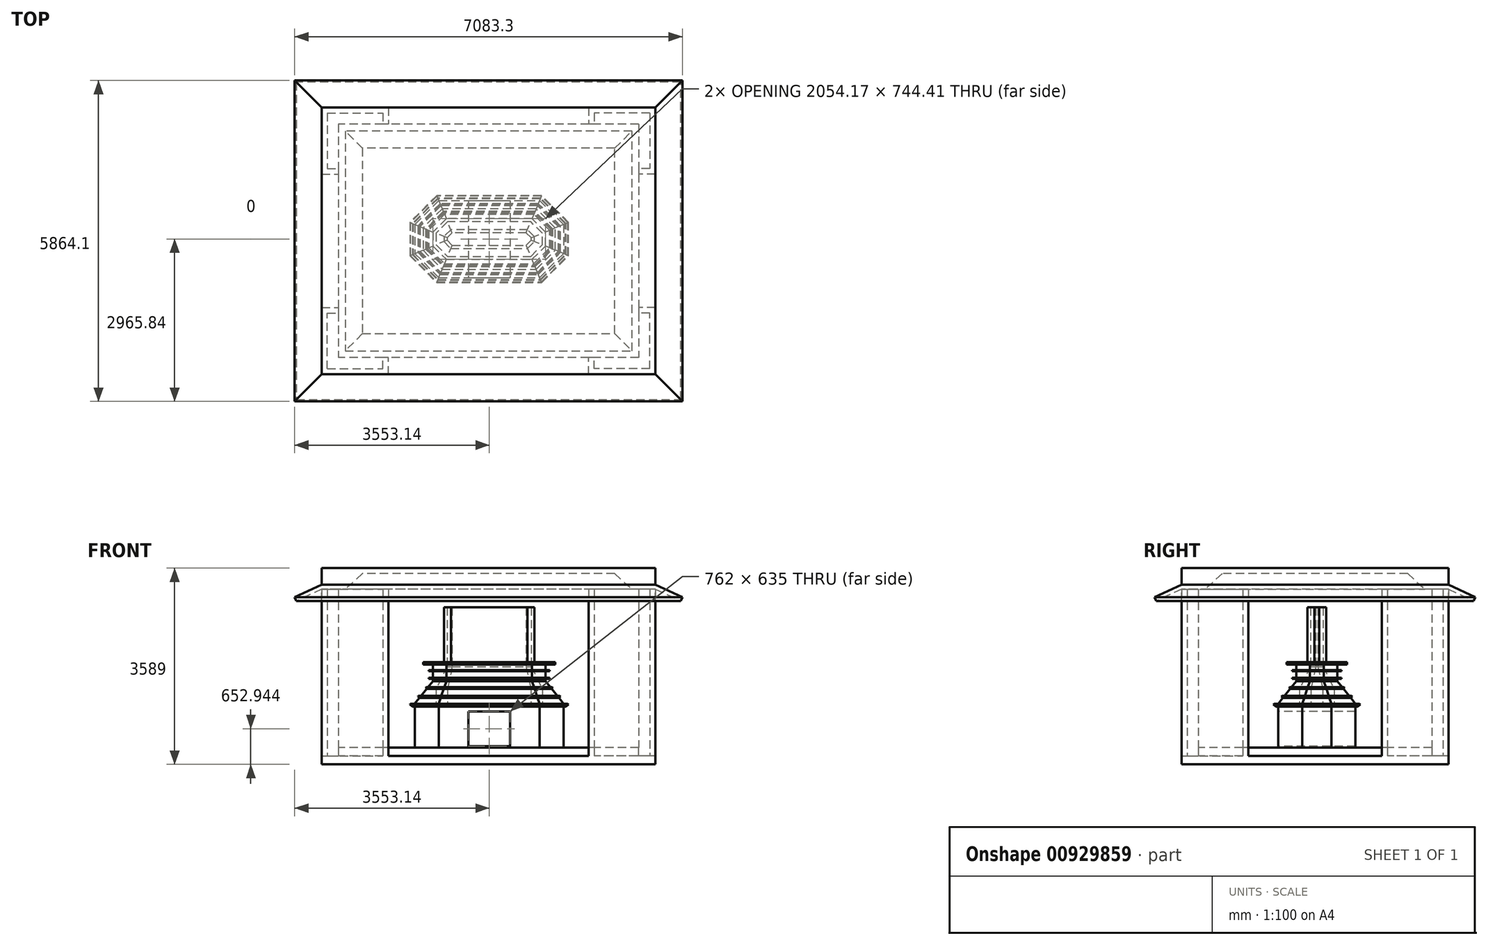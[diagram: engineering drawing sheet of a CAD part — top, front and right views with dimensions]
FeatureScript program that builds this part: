
annotation { "Feature Type Name" : "Feature", "Feature Type Description" : "" }
export const myFeature = defineFeature(function(context is Context, id is Id, definition is map)
    precondition{}
    {
        {
            var Q0;
            Q0=qCreatedBy(makeId("Right.planeOp"),FACE);
            var sketch = newSketch(context, id + "F0", { "sketchPlane" : qUnion([Q0])});
            skLineSegment(sketch, "E0", {"start": v(0, 0) * mm, "end": v(-2438.4, 0) * mm});
            skLineSegment(sketch, "E1", {"start": v(-2438.4, 0) * mm, "end": v(-2438.4, 152.4) * mm});
            skLineSegment(sketch, "E2", {"start": v(-2438.4, 152.4) * mm, "end": v(-2133.6, 152.4) * mm});
            skLineSegment(sketch, "E3", {"start": v(-2133.6, 152.4) * mm, "end": v(-2133.6, 304.8) * mm});
            skLineSegment(sketch, "E4", {"start": v(-2133.6, 304.8) * mm, "end": v(0, 304.8) * mm});
            skLineSegment(sketch, "E5", {"start": v(0, 0) * mm, "end": v(0, 304.8) * mm, "construction": true});
            skLineSegment(sketch, "E6.MirrorCS", {"start": v(0, 0) * mm, "end": v(2438.4, 0) * mm});
            skLineSegment(sketch, "E7.MirrorCS", {"start": v(2133.6, 152.4) * mm, "end": v(2133.6, 304.8) * mm});
            skLineSegment(sketch, "E8.MirrorCS", {"start": v(2438.4, 152.4) * mm, "end": v(2133.6, 152.4) * mm});
            skLineSegment(sketch, "E9.MirrorCS", {"start": v(2133.6, 304.8) * mm, "end": v(0, 304.8) * mm});
            skLineSegment(sketch, "E10.MirrorCS", {"start": v(2438.4, 0) * mm, "end": v(2438.4, 152.4) * mm});
            skPoint(sketch, "E11.trimOffspring.end.orphan", {"position": v(0, 304.8) * mm});
            skSolve(sketch);
        }
        {
            var Q0;
            Q0 = qSketchRegion(id + "F0", true);
            extrude(context, id + "F1", {"entities" : qUnion([Q0]), "depth" : 6096 * mm, "offsetDistance" : 25.4 * mm});
        }
        {
            var Q0;
            Q0=makeQuery(id+"F1.opExtrude","SWEPT_FACE",FACE,{"disambiguationData":[OSD([sQuery(id+"F0.wireOp",EDGE,"E3")])]});
            var sketch = newSketch(context, id + "F2", { "sketchPlane" : qUnion([Q0])});
            skLineSegment(sketch, "E12.bottom", {"start": v(0, 152.4) * mm, "end": v(304.8, 152.4) * mm});
            skLineSegment(sketch, "E12.top", {"start": v(0, 304.8) * mm, "end": v(304.8, 304.8) * mm});
            skLineSegment(sketch, "E12.left", {"start": v(0, 152.4) * mm, "end": v(0, 304.8) * mm});
            skLineSegment(sketch, "E12.right", {"start": v(304.8, 152.4) * mm, "end": v(304.8, 304.8) * mm});
            skLineSegment(sketch, "E13.bottom", {"start": v(6096, 152.4) * mm, "end": v(5791.2, 152.4) * mm});
            skLineSegment(sketch, "E13.top", {"start": v(6096, 304.8) * mm, "end": v(5791.2, 304.8) * mm});
            skLineSegment(sketch, "E13.left", {"start": v(6096, 152.4) * mm, "end": v(6096, 304.8) * mm});
            skLineSegment(sketch, "E13.right", {"start": v(5791.2, 152.4) * mm, "end": v(5791.2, 304.8) * mm});
            skSolve(sketch);
        }
        {
            var Q0;
            Q0=makeQuery(id+"F2.imprint","IMPRINT",FACE,{"disambiguationData":[TD([[makeQuery(id+"F2.imprint","IMPRINT",EDGE,{"derivedFrom":sQuery(id+"F2.wireOp",EDGE,"E12.bottom")}),-1.0]])]});
            var Q1;
            Q1=makeQuery(id+"F2.imprint","IMPRINT",FACE,{"disambiguationData":[TD([[makeQuery(id+"F2.imprint","IMPRINT",EDGE,{"derivedFrom":sQuery(id+"F2.wireOp",EDGE,"E13.bottom")}),-1.0]])]});
            extrude(context, id + "F3", {"entities" : qUnion([Q0, Q1]), "operationType" : NewBodyOperationType.REMOVE, "endBound" : BoundingType.THROUGH_ALL, "oppositeDirection" : true, "depth" : 25.4 * mm, "offsetDistance" : 25.4 * mm});
        }
        {
            var Q0;
            Q0=makeQuery(id+"F3.boolean.opBoolean","MERGE",FACE,{"derivedFrom":[makeQuery(id+"F1.opExtrude","SWEPT_FACE",FACE,{"disambiguationData":[OSD([sQuery(id+"F0.wireOp",EDGE,"E2")])]}),makeQuery(id+"F1.opExtrude","SWEPT_FACE",FACE,{"disambiguationData":[OSD([sQuery(id+"F0.wireOp",EDGE,"E8.MirrorCS")])]})],"fromTools":[makeQuery(id+"F3.opExtrude","SWEPT_FACE",FACE,{"disambiguationData":[OSD([sQuery(id+"F2.wireOp",EDGE,"E12.bottom")])]}),makeQuery(id+"F3.opExtrude","SWEPT_FACE",FACE,{"disambiguationData":[OSD([sQuery(id+"F2.wireOp",EDGE,"E13.bottom")])]})]});
            var sketch = newSketch(context, id + "F4", { "sketchPlane" : qUnion([Q0])});
            skLineSegment(sketch, "E14.bottom", {"start": v(0, 2438.4) * mm, "end": v(1219.2, 2438.4) * mm});
            skLineSegment(sketch, "E14.top", {"start": v(0, 1219.2) * mm, "end": v(304.8, 1219.2) * mm});
            skLineSegment(sketch, "E14.left", {"start": v(0, 2438.4) * mm, "end": v(0, 1219.2) * mm});
            skLineSegment(sketch, "E14.right", {"start": v(1219.2, 2438.4) * mm, "end": v(1219.2, 2133.6) * mm});
            skLineSegment(sketch, "E15.bottom", {"start": v(1117.6, 2133.6) * mm, "end": v(1219.2, 2133.6) * mm});
            skLineSegment(sketch, "E15.left", {"start": v(304.8, 1320.8) * mm, "end": v(304.8, 1219.2) * mm});
            skLineSegment(sketch, "E16", {"start": v(3048, 2438.4) * mm, "end": v(3048, -2438.4) * mm, "construction": true});
            skLineSegment(sketch, "E17", {"start": v(0, 0) * mm, "end": v(6096, 0) * mm, "construction": true});
            skLineSegment(sketch, "E18.MirrorCS", {"start": v(4978.4, 2133.6) * mm, "end": v(4876.8, 2133.6) * mm});
            skLineSegment(sketch, "E19.MirrorCS", {"start": v(6096, 1219.2) * mm, "end": v(5791.2, 1219.2) * mm});
            skLineSegment(sketch, "E20.MirrorCS", {"start": v(5791.2, 1320.8) * mm, "end": v(5791.2, 1219.2) * mm});
            skLineSegment(sketch, "E21.MirrorCS", {"start": v(6096, 2438.4) * mm, "end": v(6096, 1219.2) * mm});
            skLineSegment(sketch, "E22.MirrorCS", {"start": v(4876.8, 2438.4) * mm, "end": v(4876.8, 2133.6) * mm});
            skLineSegment(sketch, "E23.MirrorCS", {"start": v(6096, 2438.4) * mm, "end": v(4876.8, 2438.4) * mm});
            skLineSegment(sketch, "E24.bottom", {"start": v(101.6, 2336.8) * mm, "end": v(1117.6, 2336.8) * mm});
            skLineSegment(sketch, "E24.top", {"start": v(101.6, 1320.8) * mm, "end": v(304.8, 1320.8) * mm});
            skLineSegment(sketch, "E24.left", {"start": v(101.6, 2336.8) * mm, "end": v(101.6, 1320.8) * mm});
            skLineSegment(sketch, "E24.right", {"start": v(1117.6, 2336.8) * mm, "end": v(1117.6, 2133.6) * mm});
            skPoint(sketch, "E25.orphan", {"position": v(304.8, 2133.6) * mm});
            skLineSegment(sketch, "E26.MirrorCS", {"start": v(5994.4, 2336.8) * mm, "end": v(4978.4, 2336.8) * mm});
            skLineSegment(sketch, "E27.MirrorCS", {"start": v(5994.4, 2336.8) * mm, "end": v(5994.4, 1320.8) * mm});
            skLineSegment(sketch, "E28.MirrorCS", {"start": v(5994.4, 1320.8) * mm, "end": v(5791.2, 1320.8) * mm});
            skLineSegment(sketch, "E29.MirrorCS", {"start": v(4978.4, 2336.8) * mm, "end": v(4978.4, 2133.6) * mm});
            skPoint(sketch, "E30.orphan", {"position": v(5791.2, 2133.6) * mm});
            skLineSegment(sketch, "E31.MirrorCS", {"start": v(5994.4, -1320.8) * mm, "end": v(5791.2, -1320.8) * mm});
            skLineSegment(sketch, "E32.MirrorCS", {"start": v(1117.6, -2133.6) * mm, "end": v(1219.2, -2133.6) * mm});
            skLineSegment(sketch, "E33.MirrorCS", {"start": v(101.6, -1320.8) * mm, "end": v(304.8, -1320.8) * mm});
            skLineSegment(sketch, "E34.MirrorCS", {"start": v(1219.2, -2438.4) * mm, "end": v(1219.2, -2133.6) * mm});
            skLineSegment(sketch, "E35.MirrorCS", {"start": v(5791.2, -1320.8) * mm, "end": v(5791.2, -1219.2) * mm});
            skLineSegment(sketch, "E36.MirrorCS", {"start": v(304.8, -1320.8) * mm, "end": v(304.8, -1219.2) * mm});
            skLineSegment(sketch, "E37.MirrorCS", {"start": v(4978.4, -2336.8) * mm, "end": v(4978.4, -2133.6) * mm});
            skLineSegment(sketch, "E38.MirrorCS", {"start": v(4978.4, -2133.6) * mm, "end": v(4876.8, -2133.6) * mm});
            skLineSegment(sketch, "E39.MirrorCS", {"start": v(1117.6, -2336.8) * mm, "end": v(1117.6, -2133.6) * mm});
            skLineSegment(sketch, "E40.MirrorCS", {"start": v(6096, -2438.4) * mm, "end": v(4876.8, -2438.4) * mm});
            skPoint(sketch, "E41.MirrorP", {"position": v(304.8, -2133.6) * mm});
            skLineSegment(sketch, "E42.MirrorCS", {"start": v(6096, -2438.4) * mm, "end": v(6096, -1219.2) * mm});
            skLineSegment(sketch, "E43.MirrorCS", {"start": v(0, -2438.4) * mm, "end": v(1219.2, -2438.4) * mm});
            skLineSegment(sketch, "E44.MirrorCS", {"start": v(0, -2438.4) * mm, "end": v(0, -1219.2) * mm});
            skLineSegment(sketch, "E45.MirrorCS", {"start": v(101.6, -2336.8) * mm, "end": v(1117.6, -2336.8) * mm});
            skLineSegment(sketch, "E46.MirrorCS", {"start": v(4876.8, -2438.4) * mm, "end": v(4876.8, -2133.6) * mm});
            skLineSegment(sketch, "E47.MirrorCS", {"start": v(6096, -1219.2) * mm, "end": v(5791.2, -1219.2) * mm});
            skPoint(sketch, "E48.MirrorP", {"position": v(5791.2, -2133.6) * mm});
            skLineSegment(sketch, "E49.MirrorCS", {"start": v(101.6, -2336.8) * mm, "end": v(101.6, -1320.8) * mm});
            skLineSegment(sketch, "E50.MirrorCS", {"start": v(5994.4, -2336.8) * mm, "end": v(5994.4, -1320.8) * mm});
            skLineSegment(sketch, "E51.MirrorCS", {"start": v(0, -1219.2) * mm, "end": v(304.8, -1219.2) * mm});
            skLineSegment(sketch, "E52.MirrorCS", {"start": v(5994.4, -2336.8) * mm, "end": v(4978.4, -2336.8) * mm});
            skSolve(sketch);
        }
        {
            var Q0;
            Q0=makeQuery(id+"F4.imprint","IMPRINT",FACE,{"disambiguationData":[TD([[makeQuery(id+"F4.imprint","IMPRINT",EDGE,{"derivedFrom":sQuery(id+"F4.wireOp",EDGE,"E32.MirrorCS")}),1.0]])]});
            var Q1;
            Q1=makeQuery(id+"F4.imprint","IMPRINT",FACE,{"disambiguationData":[TD([[makeQuery(id+"F4.imprint","IMPRINT",EDGE,{"derivedFrom":sQuery(id+"F4.wireOp",EDGE,"E14.bottom")}),1.0]])]});
            var Q2;
            Q2=makeQuery(id+"F4.imprint","IMPRINT",FACE,{"disambiguationData":[TD([[makeQuery(id+"F4.imprint","IMPRINT",EDGE,{"derivedFrom":sQuery(id+"F4.wireOp",EDGE,"E31.MirrorCS")}),-1.0]])]});
            var Q3;
            Q3=makeQuery(id+"F4.imprint","IMPRINT",FACE,{"disambiguationData":[TD([[makeQuery(id+"F4.imprint","IMPRINT",EDGE,{"derivedFrom":sQuery(id+"F4.wireOp",EDGE,"E18.MirrorCS")}),-1.0]])]});
            extrude(context, id + "F5", {"entities" : qUnion([Q0, Q1, Q2, Q3]), "operationType" : NewBodyOperationType.ADD, "depth" : 3048 * mm, "offsetDistance" : 25.4 * mm});
        }
        {
            var Q0;
            Q0=makeQuery(id+"F5.opExtrude","CAP_FACE",FACE,{"disambiguationData":[OSD([sQuery(id+"F4.wireOp",EDGE,"E14.bottom"),sQuery(id+"F4.wireOp",EDGE,"E14.top"),sQuery(id+"F4.wireOp",EDGE,"E14.left"),sQuery(id+"F4.wireOp",EDGE,"E14.right"),sQuery(id+"F4.wireOp",EDGE,"E15.bottom"),sQuery(id+"F4.wireOp",EDGE,"E15.left"),sQuery(id+"F4.wireOp",EDGE,"E24.bottom"),sQuery(id+"F4.wireOp",EDGE,"E24.top"),sQuery(id+"F4.wireOp",EDGE,"E24.left"),sQuery(id+"F4.wireOp",EDGE,"E24.right")])],"isStart":false});
            var sketch = newSketch(context, id + "F6", { "sketchPlane" : qUnion([Q0])});
            skLineSegment(sketch, "E53.bottom", {"start": v(0, -2438.4) * mm, "end": v(6096, -2438.4) * mm});
            skLineSegment(sketch, "E53.top", {"start": v(0, 2438.4) * mm, "end": v(6096, 2438.4) * mm});
            skLineSegment(sketch, "E53.left", {"start": v(0, -2438.4) * mm, "end": v(0, 2438.4) * mm});
            skLineSegment(sketch, "E53.right", {"start": v(6096, -2438.4) * mm, "end": v(6096, 2438.4) * mm});
            skSolve(sketch);
        }
        {
            var Q0;
            Q0=makeQuery(id+"F5.boolean.opBoolean","MERGE",FACE,{"derivedFrom":[makeQuery(id+"F1.opExtrude","CAP_FACE",FACE,{"disambiguationData":[OSD([sQuery(id+"F0.wireOp",EDGE,"E0"),sQuery(id+"F0.wireOp",EDGE,"E1"),sQuery(id+"F0.wireOp",EDGE,"E2"),sQuery(id+"F0.wireOp",EDGE,"E3"),sQuery(id+"F0.wireOp",EDGE,"E4"),sQuery(id+"F0.wireOp",EDGE,"E6.MirrorCS"),sQuery(id+"F0.wireOp",EDGE,"E7.MirrorCS"),sQuery(id+"F0.wireOp",EDGE,"E8.MirrorCS"),sQuery(id+"F0.wireOp",EDGE,"E9.MirrorCS"),sQuery(id+"F0.wireOp",EDGE,"E10.MirrorCS")])],"isStart":false}),makeQuery(id+"F5.opExtrude","SWEPT_FACE",FACE,{"disambiguationData":[OSD([sQuery(id+"F4.wireOp",EDGE,"E21.MirrorCS")])]}),makeQuery(id+"F5.opExtrude","SWEPT_FACE",FACE,{"disambiguationData":[OSD([sQuery(id+"F4.wireOp",EDGE,"83ccc331-1453-4f70-b9a5-2f804921cb002.MirrorCS")])]})]});
            cPlane(context, id + "F7", {"entities" : qUnion([Q0]), "cplaneType" : CPlaneType.OFFSET, "offset" : 2540 * mm, "oppositeDirection" : true, "width" : 152.4 * mm, "height" : 152.4 * mm});
        }
        {
            var Q0;
            Q0=qCreatedBy(id+"F7.planeOp",FACE);
            var sketch = newSketch(context, id + "F8", { "sketchPlane" : qUnion([Q0])});
            skLineSegment(sketch, "E54", {"start": v(-2438.4, 3200.4) * mm, "end": v(-2010.27, 3200.4) * mm});
            skLineSegment(sketch, "E55", {"start": v(-2010.27, 3200.4) * mm, "end": v(-1694.53, 3487.18) * mm});
            skLineSegment(sketch, "E56", {"start": v(-1694.53, 3487.18) * mm, "end": v(0, 3487.18) * mm});
            skLineSegment(sketch, "E57", {"start": v(-2438.4, 3200.4) * mm, "end": v(-2900.35, 2989.05) * mm});
            skLineSegment(sketch, "E58", {"start": v(-2900.35, 2989.05) * mm, "end": v(-2932.05, 3058.34) * mm});
            skLineSegment(sketch, "E59", {"start": v(-2932.05, 3058.34) * mm, "end": v(-2438.4, 3284.2) * mm});
            skLineSegment(sketch, "E60", {"start": v(-2438.4, 3284.2) * mm, "end": v(-2438.4, 3589) * mm});
            skLineSegment(sketch, "E61", {"start": v(-2438.4, 3589) * mm, "end": v(-2309.08, 3589) * mm});
            skLineSegment(sketch, "E62", {"start": v(-2309.08, 3589) * mm, "end": v(0, 3589) * mm});
            skLineSegment(sketch, "E63", {"start": v(0, 3589) * mm, "end": v(0, 3487.18) * mm});
            skSolve(sketch);
        }
        {
            var Q0;
            Q0=makeQuery(id+"F8.imprint","IMPRINT",FACE,{"disambiguationData":[TD([[makeQuery(id+"F8.imprint","IMPRINT",EDGE,{"derivedFrom":sQuery(id+"F8.wireOp",EDGE,"E54")}),1.0]])]});
            var Q1;
            Q1=sQuery(id+"F6.wireOp",EDGE,"E53.bottom");
            var Q2;
            Q2=sQuery(id+"F6.wireOp",EDGE,"E53.right");
            var Q3;
            Q3=sQuery(id+"F6.wireOp",EDGE,"E53.top");
            var Q4;
            Q4=sQuery(id+"F6.wireOp",EDGE,"E53.left");
            sweep(context, id + "F9", {"profiles" : qUnion([Q0]), "path" : qUnion([Q1, Q2, Q3, Q4])});
        }
        {
            var Q0;
            Q0=makeQuery(id+"F1.opExtrude","SWEPT_FACE",FACE,{"disambiguationData":[OSD([sQuery(id+"F0.wireOp",EDGE,"E4"),sQuery(id+"F0.wireOp",EDGE,"E9.MirrorCS")])]});
            var sketch = newSketch(context, id + "F10", { "sketchPlane" : qUnion([Q0])});
            skLineSegment(sketch, "E64.bottom", {"start": v(1701.8, 736.6) * mm, "end": v(4417.2, 736.6) * mm});
            skLineSegment(sketch, "E64.top", {"start": v(1701.8, -669.03) * mm, "end": v(4417.2, -669.03) * mm});
            skLineSegment(sketch, "E64.left", {"start": v(1701.8, 736.6) * mm, "end": v(1701.8, -669.03) * mm});
            skLineSegment(sketch, "E64.right", {"start": v(4417.2, 736.6) * mm, "end": v(4417.2, -669.03) * mm});
            skLineSegment(sketch, "E65", {"start": v(2139.34, 736.6) * mm, "end": v(1701.8, 299.06) * mm});
            skLineSegment(sketch, "E66", {"start": v(3059.5, 736.6) * mm, "end": v(3059.5, -669.03) * mm, "construction": true});
            skLineSegment(sketch, "E67", {"start": v(4417.2, 33.79) * mm, "end": v(1701.8, 33.79) * mm, "construction": true});
            skLineSegment(sketch, "E68.MirrorCS", {"start": v(3979.65, 736.6) * mm, "end": v(4417.2, 299.06) * mm});
            skLineSegment(sketch, "E69.MirrorCS", {"start": v(2139.34, -669.03) * mm, "end": v(1701.8, -231.48) * mm});
            skLineSegment(sketch, "E70.MirrorCS", {"start": v(3979.65, -669.03) * mm, "end": v(4417.2, -231.48) * mm});
            skSolve(sketch);
        }
        {
            var Q0;
            {var subQ3=sQuery(id+"F10.wireOp",EDGE,"E65");Q0=makeQuery(id+"F10.imprint","IMPRINT",FACE,{"disambiguationData":[TD([[makeQuery(id+"F10.imprint","IMPRINT",EDGE,{"derivedFrom":subQ3}),1.0]])]});}
            extrude(context, id + "F11", {"entities" : qUnion([Q0]), "depth" : 762 * mm, "offsetDistance" : 25.4 * mm});
        }
        {
            var Q0;
            Q0=makeQuery(id+"F11.opExtrude","SWEPT_FACE",FACE,{"disambiguationData":[OSD([sQuery(id+"F10.wireOp",EDGE,"E64.right")])]});
            cPlane(context, id + "F12", {"entities" : qUnion([Q0]), "cplaneType" : CPlaneType.OFFSET, "offset" : 1016 * mm, "oppositeDirection" : true, "width" : 152.4 * mm, "height" : 152.4 * mm});
        }
        {
            var Q0;
            Q0=qCreatedBy(id+"F12.planeOp",FACE);
            var sketch = newSketch(context, id + "F13", { "sketchPlane" : qUnion([Q0])});
            skLineSegment(sketch, "E71", {"start": v(-715.62, 1058.13) * mm, "end": v(-338.42, 1058.13) * mm});
            skLineSegment(sketch, "E72", {"start": v(-338.42, 1058.13) * mm, "end": v(-338.42, 1522.92) * mm});
            skLineSegment(sketch, "E73", {"start": v(-338.42, 1522.92) * mm, "end": v(-715.62, 1058.13) * mm});
            skLineSegment(sketch, "E74", {"start": v(-338.42, 1522.92) * mm, "end": v(-338.42, 1824.94) * mm});
            skLineSegment(sketch, "E75", {"start": v(-338.42, 1824.94) * mm, "end": v(-283.36, 1824.94) * mm});
            skLineSegment(sketch, "E76", {"start": v(-283.36, 1824.94) * mm, "end": v(-283.36, 1058.13) * mm});
            skLineSegment(sketch, "E77", {"start": v(-283.36, 1058.13) * mm, "end": v(-338.42, 1058.13) * mm});
            skLineSegment(sketch, "E78", {"start": v(-338.42, 1824.94) * mm, "end": v(-519.63, 1824.94) * mm});
            skLineSegment(sketch, "E79", {"start": v(-519.63, 1824.94) * mm, "end": v(-519.63, 1871.13) * mm});
            skLineSegment(sketch, "E80", {"start": v(-519.63, 1871.13) * mm, "end": v(-283.36, 1871.13) * mm});
            skLineSegment(sketch, "E81", {"start": v(-283.36, 1871.13) * mm, "end": v(-283.36, 1824.94) * mm});
            skLineSegment(sketch, "E82", {"start": v(-715.62, 1058.13) * mm, "end": v(-761.51, 1095.37) * mm});
            skLineSegment(sketch, "E83", {"start": v(-761.51, 1095.37) * mm, "end": v(-749.51, 1110.17) * mm});
            skLineSegment(sketch, "E84", {"start": v(-749.51, 1110.17) * mm, "end": v(-703.62, 1072.92) * mm});
            skLineSegment(sketch, "E85", {"start": v(-586.2, 1217.6) * mm, "end": v(-615.17, 1241.1) * mm});
            skLineSegment(sketch, "E86", {"start": v(-615.17, 1241.1) * mm, "end": v(-603.16, 1255.9) * mm});
            skLineSegment(sketch, "E87", {"start": v(-603.16, 1255.9) * mm, "end": v(-574.2, 1232.39) * mm});
            skLineSegment(sketch, "E88", {"start": v(-453.2, 1381.47) * mm, "end": v(-471.43, 1396.26) * mm});
            skLineSegment(sketch, "E89", {"start": v(-471.43, 1396.26) * mm, "end": v(-459.43, 1411.05) * mm});
            skLineSegment(sketch, "E90", {"start": v(-459.43, 1411.05) * mm, "end": v(-441.2, 1396.26) * mm});
            skLineSegment(sketch, "E91.bottom", {"start": v(-338.42, 1563.22) * mm, "end": v(-416.6, 1563.22) * mm});
            skLineSegment(sketch, "E91.top", {"start": v(-338.42, 1582.27) * mm, "end": v(-416.6, 1582.27) * mm});
            skLineSegment(sketch, "E91.left", {"start": v(-338.42, 1563.22) * mm, "end": v(-338.42, 1582.27) * mm});
            skLineSegment(sketch, "E91.right", {"start": v(-416.6, 1563.22) * mm, "end": v(-416.6, 1582.27) * mm});
            skLineSegment(sketch, "E92.bottom", {"start": v(-338.42, 1702.1) * mm, "end": v(-416.6, 1702.1) * mm});
            skLineSegment(sketch, "E92.top", {"start": v(-338.42, 1721.16) * mm, "end": v(-416.6, 1721.16) * mm});
            skLineSegment(sketch, "E92.left", {"start": v(-338.42, 1702.1) * mm, "end": v(-338.42, 1721.16) * mm});
            skLineSegment(sketch, "E92.right", {"start": v(-416.6, 1702.1) * mm, "end": v(-416.6, 1721.16) * mm});
            skLineSegment(sketch, "E93", {"start": v(-283.36, 1871.13) * mm, "end": v(-138.53, 1871.13) * mm});
            skLineSegment(sketch, "E94", {"start": v(-138.53, 1871.13) * mm, "end": v(-138.53, 2870.43) * mm});
            skLineSegment(sketch, "E95", {"start": v(-138.53, 2870.43) * mm, "end": v(-79.83, 2870.43) * mm});
            skLineSegment(sketch, "E96", {"start": v(-79.83, 2870.43) * mm, "end": v(-79.83, 1784.64) * mm});
            skLineSegment(sketch, "E97", {"start": v(-79.83, 1784.64) * mm, "end": v(-283.36, 1383.1) * mm});
            skSolve(sketch);
        }
        {
            var Q0;
            Q0=makeQuery(id+"F13.imprint","IMPRINT",FACE,{"disambiguationData":[TD([[makeQuery(id+"F13.imprint","IMPRINT",EDGE,{"derivedFrom":sQuery(id+"F13.wireOp",EDGE,"E75")}),1.0]])]});
            var Q1;
            {var subQ1=sQuery(id+"F13.wireOp",EDGE,"E72");Q1=makeQuery(id+"F13.imprint","IMPRINT",FACE,{"disambiguationData":[TD([[makeQuery(id+"F13.imprint","IMPRINT",EDGE,{"derivedFrom":subQ1}),-1.0]])]});}
            var Q2;
            {var subQ2=sQuery(id+"F13.wireOp",EDGE,"E92.bottom");Q2=makeQuery(id+"F13.imprint","IMPRINT",FACE,{"disambiguationData":[TD([[makeQuery(id+"F13.imprint","IMPRINT",EDGE,{"derivedFrom":subQ2}),-1.0]])]});}
            var Q3;
            {var subQ2=sQuery(id+"F13.wireOp",EDGE,"E91.bottom");Q3=makeQuery(id+"F13.imprint","IMPRINT",FACE,{"disambiguationData":[TD([[makeQuery(id+"F13.imprint","IMPRINT",EDGE,{"derivedFrom":subQ2}),-1.0]])]});}
            var Q4;
            {var subQ6=sQuery(id+"F13.wireOp",EDGE,"E71");Q4=makeQuery(id+"F13.imprint","IMPRINT",FACE,{"disambiguationData":[TD([[makeQuery(id+"F13.imprint","IMPRINT",EDGE,{"derivedFrom":subQ6}),1.0]])]});}
            var Q5;
            {var subQ0=sQuery(id+"F13.wireOp",EDGE,"E85");Q5=makeQuery(id+"F13.imprint","IMPRINT",FACE,{"disambiguationData":[TD([[makeQuery(id+"F13.imprint","IMPRINT",EDGE,{"derivedFrom":subQ0}),-1.0]])]});}
            var Q6;
            {var subQ0=sQuery(id+"F13.wireOp",EDGE,"E82");Q6=makeQuery(id+"F13.imprint","IMPRINT",FACE,{"disambiguationData":[TD([[makeQuery(id+"F13.imprint","IMPRINT",EDGE,{"derivedFrom":subQ0}),-1.0]])]});}
            var Q7;
            {var subQ0=sQuery(id+"F13.wireOp",EDGE,"E88");Q7=makeQuery(id+"F13.imprint","IMPRINT",FACE,{"disambiguationData":[TD([[makeQuery(id+"F13.imprint","IMPRINT",EDGE,{"derivedFrom":subQ0}),-1.0]])]});}
            var Q8;
            {var subQ0=sQuery(id+"F13.wireOp",EDGE,"E81");Q8=makeQuery(id+"F13.imprint","IMPRINT",FACE,{"disambiguationData":[TD([[makeQuery(id+"F13.imprint","IMPRINT",EDGE,{"derivedFrom":subQ0}),1.0]])]});}
            var Q9;
            Q9=makeQuery(id+"F11.opExtrude","CAP_EDGE",EDGE,{"disambiguationData":[OSD([sQuery(id+"F10.wireOp",EDGE,"E64.top")])],"isStart":false});
            var Q10;
            Q10=makeQuery(id+"F11.opExtrude","CAP_EDGE",EDGE,{"disambiguationData":[OSD([sQuery(id+"F10.wireOp",EDGE,"E70.MirrorCS")])],"isStart":false});
            var Q11;
            Q11=makeQuery(id+"F11.opExtrude","CAP_EDGE",EDGE,{"disambiguationData":[OSD([sQuery(id+"F10.wireOp",EDGE,"E64.right")])],"isStart":false});
            var Q12;
            Q12=makeQuery(id+"F11.opExtrude","CAP_EDGE",EDGE,{"disambiguationData":[OSD([sQuery(id+"F10.wireOp",EDGE,"E68.MirrorCS")])],"isStart":false});
            var Q13;
            Q13=makeQuery(id+"F11.opExtrude","CAP_EDGE",EDGE,{"disambiguationData":[OSD([sQuery(id+"F10.wireOp",EDGE,"E64.bottom")])],"isStart":false});
            var Q14;
            Q14=makeQuery(id+"F11.opExtrude","CAP_EDGE",EDGE,{"disambiguationData":[OSD([sQuery(id+"F10.wireOp",EDGE,"E65")])],"isStart":false});
            var Q15;
            Q15=makeQuery(id+"F11.opExtrude","CAP_EDGE",EDGE,{"disambiguationData":[OSD([sQuery(id+"F10.wireOp",EDGE,"E64.left")])],"isStart":false});
            var Q16;
            Q16=makeQuery(id+"F11.opExtrude","CAP_EDGE",EDGE,{"disambiguationData":[OSD([sQuery(id+"F10.wireOp",EDGE,"E69.MirrorCS")])],"isStart":false});
            sweep(context, id + "F14", {"profiles" : qUnion([Q0, Q1, Q2, Q3, Q4, Q5, Q6, Q7, Q8]), "path" : qUnion([Q9, Q10, Q11, Q12, Q13, Q14, Q15, Q16])});
        }
        {
            var Q0;
            Q0=makeQuery(id+"F11.opExtrude","SWEPT_FACE",FACE,{"disambiguationData":[OSD([sQuery(id+"F10.wireOp",EDGE,"E64.top")])]});
            var sketch = newSketch(context, id + "F15", { "sketchPlane" : qUnion([Q0])});
            skLineSegment(sketch, "E98.bottom", {"start": v(2678.5, 970.44) * mm, "end": v(3440.5, 970.44) * mm});
            skLineSegment(sketch, "E98.top", {"start": v(2678.5, 335.44) * mm, "end": v(3440.5, 335.44) * mm});
            skLineSegment(sketch, "E98.left", {"start": v(2678.5, 970.44) * mm, "end": v(2678.5, 335.44) * mm});
            skLineSegment(sketch, "E98.right", {"start": v(3440.5, 970.44) * mm, "end": v(3440.5, 335.44) * mm});
            skLineSegment(sketch, "E99", {"start": v(3059.5, 1066.8) * mm, "end": v(3059.5, 869.3) * mm, "construction": true});
            skSolve(sketch);
        }
        {
            var Q0;
            Q0=makeQuery(id+"F15.imprint","IMPRINT",FACE,{"disambiguationData":[TD([[makeQuery(id+"F15.imprint","IMPRINT",EDGE,{"derivedFrom":sQuery(id+"F15.wireOp",EDGE,"E98.bottom")}),-1.0]])]});
            extrude(context, id + "F16", {"entities" : qUnion([Q0]), "operationType" : NewBodyOperationType.REMOVE, "endBound" : BoundingType.UP_TO_NEXT, "oppositeDirection" : true, "depth" : 25.4 * mm, "offsetDistance" : 25.4 * mm});
        }
    });
